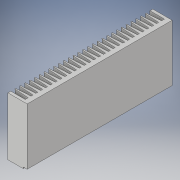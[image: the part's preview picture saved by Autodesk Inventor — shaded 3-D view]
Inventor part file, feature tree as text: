
AUTODESK INVENTOR PART (.ipt)
format: ipt  version: 2019 (Build 230136000, 136)  size: 318,464 bytes
history: native  units: mm
features: extrude x4, sketch x4, projected_geometry x2, other x1, pattern_linear x1
ambient origin geometry x8: Origin, YZ Plane, XZ Plane, XY Plane, X Axis, Y Axis, Z Axis, Center Point
bodies: Body1 (feature_tree)
feature tree (12):
  other  "Těleso1"
  extrude  "Vysunutí1"  Depth=40.0mm
  extrude  "Vysunutí2"  Depth=6.0mm
  pattern_linear  "Obdélníkové pole1"  Spacing1=2.5mm  [1 undecoded]
  extrude  "Vysunutí3"  Depth=10.0mm
  extrude  "Vysunutí5"  Depth=15.0mm
  sketch  "Náčrt1"
  sketch  "Náčrt2"
  projected_geometry  "Promítnutá smyčka1"
  sketch  "Náčrt3"
  projected_geometry  "Promítnutá smyčka2"
  sketch  "Náčrt4"
note: 1 required parameter value undecoded (feature->parameter linkage not recoverable at this tier; creation-order binding heuristic only, values carry confidence <= 0.55)
